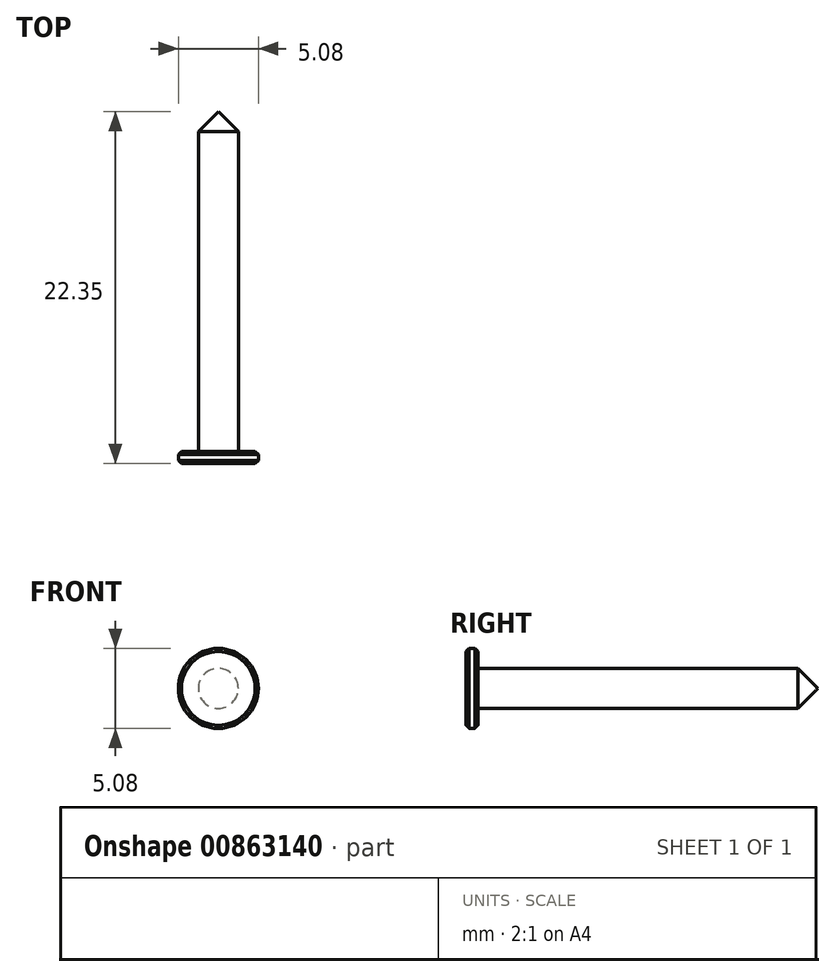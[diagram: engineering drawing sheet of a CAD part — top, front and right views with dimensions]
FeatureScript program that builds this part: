
annotation { "Feature Type Name" : "Feature", "Feature Type Description" : "" }
export const myFeature = defineFeature(function(context is Context, id is Id, definition is map)
    precondition{}
    {
        {
            var Q0;
            Q0=qCreatedBy(makeId("Front.planeOp"),FACE);
            var sketch = newSketch(context, id + "F0", { "sketchPlane" : qUnion([Q0])});
            skCircle(sketch, "E0", {"center": v(0, 0) * mm, "radius": 1.27 * mm});
            skSolve(sketch);
        }
        {
            var Q0;
            Q0=makeQuery(id+"F0.imprint","IMPRINT",FACE,{"disambiguationData":[TD([[makeQuery(id+"F0.imprint","IMPRINT",EDGE,{"derivedFrom":sQuery(id+"F0.wireOp",EDGE,"E0")}),1.0]])]});
            extrude(context, id + "F1", {"entities" : qUnion([Q0]), "depth" : 20.32 * mm, "offsetDistance" : 25.4 * mm});
        }
        {
            var Q0;
            Q0=makeQuery(id+"F1.opExtrude","CAP_FACE",FACE,{"disambiguationData":[OSD([sQuery(id+"F0.wireOp",EDGE,"E0")])],"isStart":false});
            var sketch = newSketch(context, id + "F2", { "sketchPlane" : qUnion([Q0])});
            skCircle(sketch, "E1", {"center": v(0, 0) * mm, "radius": 2.54 * mm});
            skSolve(sketch);
        }
        {
            var Q0;
            Q0=makeQuery(id+"F2.imprint","IMPRINT",FACE,{"disambiguationData":[TD([[makeQuery(id+"F2.imprint","IMPRINT",EDGE,{"derivedFrom":sQuery(id+"F2.wireOp",EDGE,"E1")}),1.0]])]});
            var Q1;
            Q1=makeQuery(id+"F2.imprint","IMPRINT",FACE,{"disambiguationData":[TD([[makeQuery(id+"F2.imprint","IMPRINT",EDGE,{"derivedFrom":makeQuery(id+"F1.opExtrude","CAP_EDGE",EDGE,{"disambiguationData":[OSD([sQuery(id+"F0.wireOp",EDGE,"E0")])],"isStart":false})}),1.0]])]});
            extrude(context, id + "F3", {"entities" : qUnion([Q0, Q1]), "depth" : 0.76 * mm, "offsetDistance" : 25.4 * mm});
        }
        {
            var Q0;
            Q0=makeQuery(id+"F3.opExtrude","CAP_EDGE",EDGE,{"disambiguationData":[OSD([sQuery(id+"F2.wireOp",EDGE,"E1")])],"isStart":false});
            var Q1;
            Q1=makeQuery(id+"F3.opExtrude","CAP_EDGE",EDGE,{"disambiguationData":[OSD([sQuery(id+"F2.wireOp",EDGE,"E1")])],"isStart":true});
            chamfer(context, id + "F4", {"entities" : qUnion([Q0, Q1]), "width" : 0.2 * mm, "tangentPropagation" : true});
        }
        {
            var Q0;
            Q0=qCreatedBy(makeId("Top.planeOp"),FACE);
            var sketch = newSketch(context, id + "F5", { "sketchPlane" : qUnion([Q0])});
            skLineSegment(sketch, "E2", {"start": v(0, 0) * mm, "end": v(0, 1.27) * mm});
            skLineSegment(sketch, "E3", {"start": v(0, 1.27) * mm, "end": v(1.27, 0) * mm});
            skLineSegment(sketch, "E4", {"start": v(0, 0) * mm, "end": v(1.27, 0) * mm});
            skSolve(sketch);
        }
        {
            var Q0;
            Q0=makeQuery(id+"F5.imprint","IMPRINT",FACE,{"disambiguationData":[TD([[makeQuery(id+"F5.imprint","IMPRINT",EDGE,{"derivedFrom":sQuery(id+"F5.wireOp",EDGE,"E2")}),-1.0]])]});
            var Q1;
            Q1=sQuery(id+"F5.wireOp",EDGE,"E2");
            revolve(context, id + "F6", {"operationType" : NewBodyOperationType.ADD, "surfaceOperationType" : NewSurfaceOperationType.NEW, "entities" : qUnion([Q0]), "axis" : qUnion([Q1]), "revolveType" : RevolveType.FULL});
        }
    });
